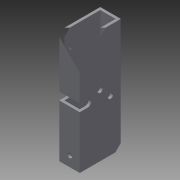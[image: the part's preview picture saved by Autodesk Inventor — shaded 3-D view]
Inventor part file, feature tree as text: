
AUTODESK INVENTOR PART (.ipt)
format: ipt  version: 2015 (Build 190159000, 159)  size: 127,488 bytes
history: native  units: in
note: dims shown in document units (in); Inventor stores cm internally (conversion verified against a paired STEP export)
features: sketch x4, extrude x2, hole x2, projected_geometry x2
ambient origin geometry x8: Origin, YZ Plane, XZ Plane, XY Plane, X Axis, Y Axis, Z Axis, Center Point
bodies: Solid1 (feature_tree)
feature tree (10):
  extrude  "Extrusion1"  Depth=2.0in
  hole  "Hole1"  [1 undecoded]
  extrude  "Extrusion2"  Depth=0.125in
  hole  "Hole2"  [1 undecoded]
  sketch  "Sketch1"  dims[d0=1.0in d1=2.0in]
  sketch  "Sketch2"  dims[d2=0.75in d3=1.75in]
  projected_geometry  "Projected Loop1"
  sketch  "Sketch3"  dims[d4=0.125in d5=0.125in]
  projected_geometry  "Projected Loop2"
  sketch  "Sketch4"  dims[d6=5.5in d7=0.0in d8=0.5in d9=0.5in d10=0.5in d11=0.5in d12=0.25in d13=0.75in d14=0.375in d15=0.25in d16=0.5635in d17=1.0in d18=0.8108in d19=2.75in d20=0.375in d21=0.375in d22=6.125in d23=0.0in d24=0.5in d25=0.5in d26=2.5in d27=0.5in d28=0.25in d29=0.75in d30=0.375in d31=0.25in d32=0.5635in d33=1.0in d34=0.8108in]
note: 2 required parameter values undecoded (feature->parameter linkage not recoverable at this tier; creation-order binding heuristic only, values carry confidence <= 0.55)
